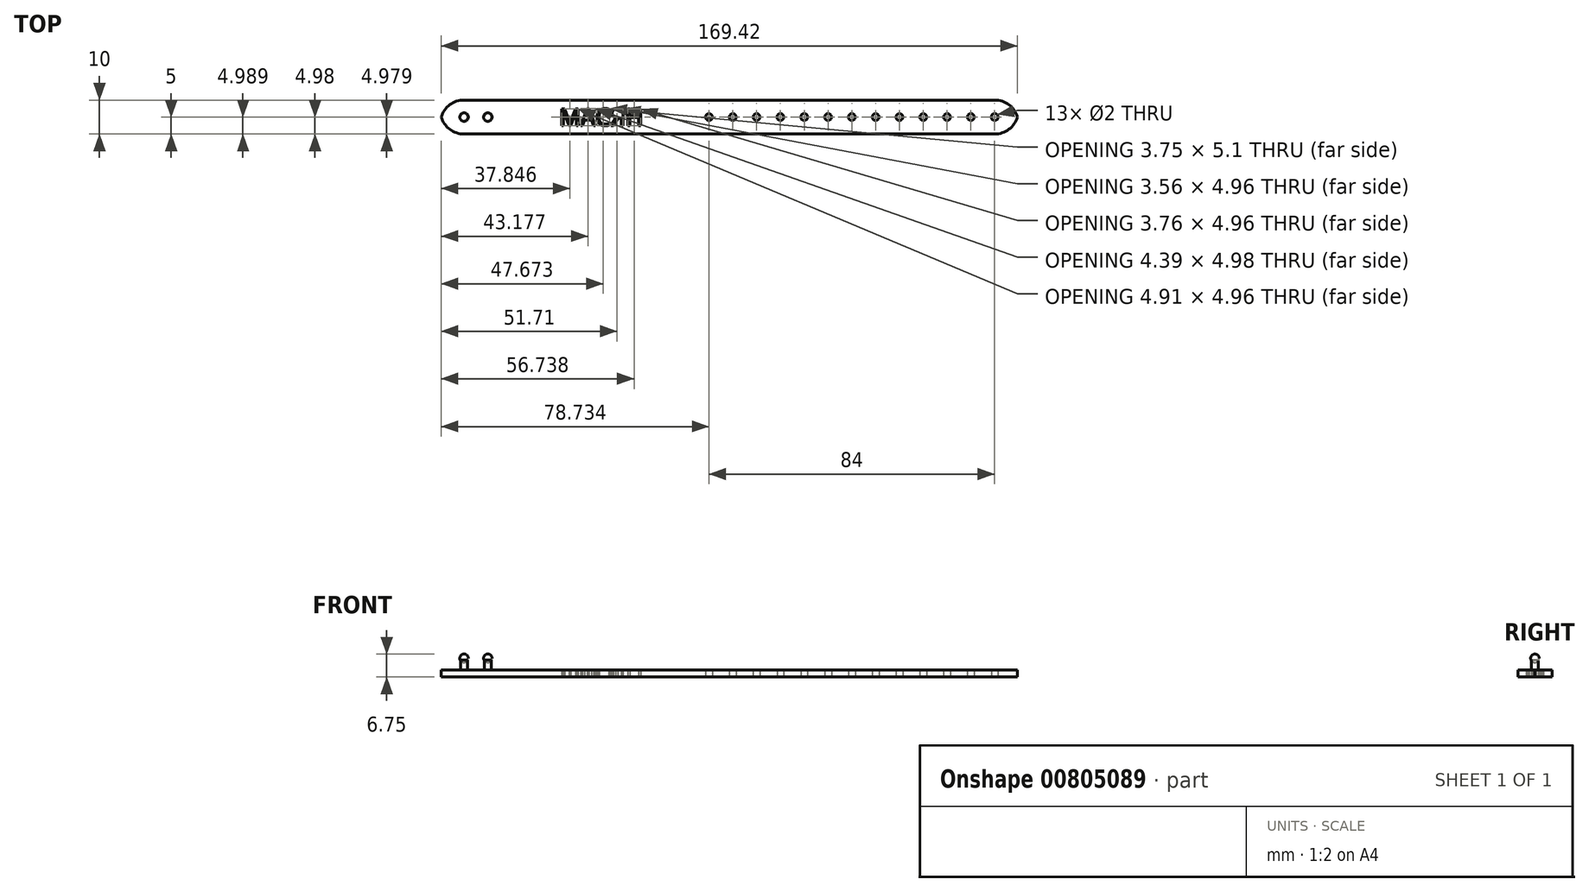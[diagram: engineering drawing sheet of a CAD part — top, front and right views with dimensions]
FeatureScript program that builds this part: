
annotation { "Feature Type Name" : "Feature", "Feature Type Description" : "" }
export const myFeature = defineFeature(function(context is Context, id is Id, definition is map)
    precondition{}
    {
        {
            var Q0;
            Q0=qCreatedBy(makeId("Top.planeOp"),FACE);
            var sketch = newSketch(context, id + "F0", { "sketchPlane" : qUnion([Q0])});
            skLineSegment(sketch, "E0.bottom", {"start": v(7, 0) * mm, "end": v(163, 0) * mm});
            skLineSegment(sketch, "E0.top", {"start": v(7, 10) * mm, "end": v(163, 10) * mm});
            skLineSegment(sketch, "E0.left", {"start": v(0, 3) * mm, "end": v(0, 7) * mm});
            skLineSegment(sketch, "E0.right", {"start": v(170, 3) * mm, "end": v(170, 7) * mm});
            skPoint(sketch, "E1.visualSharp", {"position": v(0, 10) * mm});
            skArc(sketch, "E1.filletArc", {"start": v(7, 10) * mm, "mid": v(2.05, 7.95) * mm, "end": v(0, 3) * mm});
            skPoint(sketch, "E2.visualSharp", {"position": v(170, 10) * mm});
            skArc(sketch, "E2.filletArc", {"start": v(170, 3) * mm, "mid": v(167.95, 7.95) * mm, "end": v(163, 10) * mm});
            skPoint(sketch, "E3.visualSharp", {"position": v(170, 0) * mm});
            skArc(sketch, "E3.filletArc", {"start": v(163, 0) * mm, "mid": v(167.95, 2.05) * mm, "end": v(170, 7) * mm});
            skPoint(sketch, "E4.visualSharp", {"position": v(0, 0) * mm});
            skArc(sketch, "E4.filletArc", {"start": v(0, 7) * mm, "mid": v(2.05, 2.05) * mm, "end": v(7, 0) * mm});
            skCircle(sketch, "E5", {"center": v(79.02, 5) * mm, "radius": 1 * mm});
            skCircle(sketch, "E6.1.0.0", {"center": v(86.02, 5) * mm, "radius": 1 * mm});
            skCircle(sketch, "E6.2.0.0", {"center": v(93.02, 5) * mm, "radius": 1 * mm});
            skCircle(sketch, "E6.3.0.0", {"center": v(100.02, 5) * mm, "radius": 1 * mm});
            skCircle(sketch, "E6.4.0.0", {"center": v(107.02, 5) * mm, "radius": 1 * mm});
            skCircle(sketch, "E6.5.0.0", {"center": v(114.02, 5) * mm, "radius": 1 * mm});
            skCircle(sketch, "E6.6.0.0", {"center": v(121.02, 5) * mm, "radius": 1 * mm});
            skCircle(sketch, "E6.7.0.0", {"center": v(128.02, 5) * mm, "radius": 1 * mm});
            skCircle(sketch, "E6.8.0.0", {"center": v(135.02, 5) * mm, "radius": 1 * mm});
            skCircle(sketch, "E6.9.0.0", {"center": v(142.02, 5) * mm, "radius": 1 * mm});
            skCircle(sketch, "E6.10.0.0", {"center": v(149.02, 5) * mm, "radius": 1 * mm});
            skCircle(sketch, "E6.11.0.0", {"center": v(156.02, 5) * mm, "radius": 1 * mm});
            skLineSegment(sketch, "E6.direction1", {"start": v(79.02, 5) * mm, "end": v(86.02, 5) * mm, "construction": true});
            skCircle(sketch, "E7.0.12.0", {"center": v(163.02, 5) * mm, "radius": 1 * mm});
            skText(sketch, "E8", { "text": "МАСЯН", "fontName": "OpenSans-Regular.ttf"});
            const initialGuessF0  = {"E8": [0.035, 0.0025, 1, 0, 0.005]};
            skSetInitialGuess(sketch, initialGuessF0);
            skSolve(sketch);
        }
        {
            var Q0;
            Q0 = qSketchRegion(id + "F0", true);
            extrude(context, id + "F1", {"entities" : qUnion([Q0]), "depth" : 2 * mm, "offsetDistance" : 25 * mm});
        }
        {
            var Q0;
            Q0=makeQuery(id+"F1.opExtrude","CAP_FACE",FACE,{"disambiguationData":[OSD([sQuery(id+"F0.wireOp",EDGE,"E0.bottom"),sQuery(id+"F0.wireOp",EDGE,"E0.top"),sQuery(id+"F0.wireOp",EDGE,"E1.filletArc"),sQuery(id+"F0.wireOp",EDGE,"E2.filletArc"),sQuery(id+"F0.wireOp",EDGE,"E3.filletArc"),sQuery(id+"F0.wireOp",EDGE,"E4.filletArc"),sQuery(id+"F0.wireOp",EDGE,"E5"),sQuery(id+"F0.wireOp",EDGE,"E6.1.0.0"),sQuery(id+"F0.wireOp",EDGE,"E6.2.0.0"),sQuery(id+"F0.wireOp",EDGE,"E6.3.0.0"),sQuery(id+"F0.wireOp",EDGE,"E6.4.0.0"),sQuery(id+"F0.wireOp",EDGE,"E6.5.0.0"),sQuery(id+"F0.wireOp",EDGE,"E6.6.0.0"),sQuery(id+"F0.wireOp",EDGE,"E6.7.0.0"),sQuery(id+"F0.wireOp",EDGE,"E6.8.0.0"),sQuery(id+"F0.wireOp",EDGE,"E6.9.0.0"),sQuery(id+"F0.wireOp",EDGE,"E6.10.0.0"),sQuery(id+"F0.wireOp",EDGE,"E6.11.0.0"),sQuery(id+"F0.wireOp",EDGE,"E7.0.12.0")])],"isStart":false});
            var sketch = newSketch(context, id + "F2", { "sketchPlane" : qUnion([Q0])});
            skCircle(sketch, "E9", {"center": v(7, 5) * mm, "radius": 1 * mm});
            skCircle(sketch, "E10.1.0.0", {"center": v(14, 5) * mm, "radius": 1 * mm});
            skLineSegment(sketch, "E10.direction1", {"start": v(7, 5) * mm, "end": v(14, 5) * mm, "construction": true});
            skSolve(sketch);
        }
        {
            var Q0;
            Q0 = qSketchRegion(id + "F2", true);
            extrude(context, id + "F3", {"entities" : qUnion([Q0]), "operationType" : NewBodyOperationType.ADD, "depth" : 3 * mm, "offsetDistance" : 25 * mm});
        }
        {
            var Q0;
            Q0=makeQuery(id+"F1.opExtrude","SWEPT_BODY",BODY,{"disambiguationData":[OSD([sQuery(id+"F0.wireOp",EDGE,"E0.left"),sQuery(id+"F0.wireOp",EDGE,"E1.filletArc"),sQuery(id+"F0.wireOp",EDGE,"E4.filletArc")])]});
            var Q1;
            Q1=makeQuery(id+"F1.opExtrude","SWEPT_BODY",BODY,{"disambiguationData":[OSD([sQuery(id+"F0.wireOp",EDGE,"E0.right"),sQuery(id+"F0.wireOp",EDGE,"E2.filletArc"),sQuery(id+"F0.wireOp",EDGE,"E3.filletArc")])]});
            deleteBodies(context, id + "F4", {"entities" : qUnion([Q0, Q1])});
        }
        {
            var Q0;
            Q0=makeQuery(id+"F3.opExtrude","CAP_FACE",FACE,{"disambiguationData":[OSD([sQuery(id+"F2.wireOp",EDGE,"E9")])],"isStart":false});
            cPlane(context, id + "F5", {"entities" : qUnion([Q0]), "cplaneType" : CPlaneType.OFFSET, "offset" : 0.5 * mm, "width" : 150 * mm, "height" : 150 * mm});
        }
        {
            var Q0;
            Q0=qCreatedBy(id+"F5.planeOp",FACE);
            var sketch = newSketch(context, id + "F6", { "sketchPlane" : qUnion([Q0])});
            skCircle(sketch, "E11", {"center": v(7, 5) * mm, "radius": 1.25 * mm});
            skLineSegment(sketch, "E12", {"start": v(5.75, 5) * mm, "end": v(8.25, 5) * mm});
            skSolve(sketch);
        }
        {
            var Q0;
            {var subQ0=sQuery(id+"F6.wireOp",EDGE,"E12");Q0=makeQuery(id+"F6.imprint","IMPRINT",FACE,{"disambiguationData":[TD([[makeQuery(id+"F6.imprint","IMPRINT",EDGE,{"derivedFrom":subQ0}),1.0]])]});}
            var Q1;
            Q1=makeQuery(id+"F6.imprint","IMPRINT",FACE,{"disambiguationData":[TD([[makeQuery(id+"F6.imprint","IMPRINT",EDGE,{"derivedFrom":sQuery(id+"F6.wireOp",EDGE,"58565161-7db7-4f05-a5ed-64f645377bd2.1.0.0")}),1.0]])]});
            var Q2;
            Q2=sQuery(id+"F6.wireOp",EDGE,"E12");
            revolve(context, id + "F7", {"surfaceOperationType" : NewSurfaceOperationType.NEW, "entities" : qUnion([Q0, Q1]), "axis" : qUnion([Q2]), "revolveType" : RevolveType.FULL});
        }
        {
            var Q0;
            Q0=qCreatedBy(id+"F5.planeOp",FACE);
            var sketch = newSketch(context, id + "F8", { "sketchPlane" : qUnion([Q0])});
            skCircle(sketch, "E13", {"center": v(14, 5) * mm, "radius": 1.25 * mm});
            skLineSegment(sketch, "E14", {"start": v(12.75, 5) * mm, "end": v(15.25, 5) * mm});
            skSolve(sketch);
        }
        {
            var Q0;
            {var subQ0=sQuery(id+"F8.wireOp",EDGE,"E14");Q0=makeQuery(id+"F8.imprint","IMPRINT",FACE,{"disambiguationData":[TD([[makeQuery(id+"F8.imprint","IMPRINT",EDGE,{"derivedFrom":subQ0}),1.0]])]});}
            var Q1;
            Q1=sQuery(id+"F8.wireOp",EDGE,"E14");
            revolve(context, id + "F9", {"surfaceOperationType" : NewSurfaceOperationType.NEW, "entities" : qUnion([Q0]), "axis" : qUnion([Q1]), "revolveType" : RevolveType.FULL});
        }
    });
